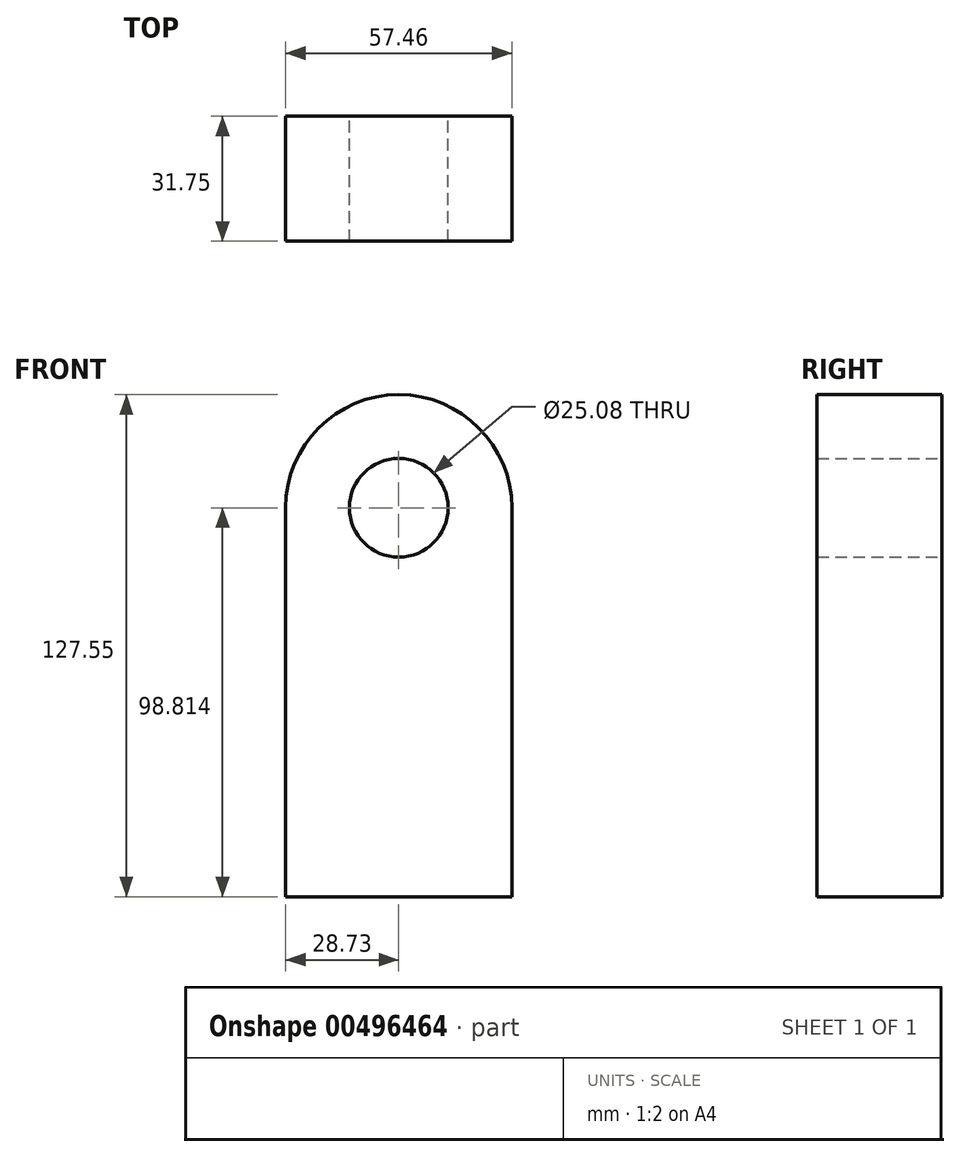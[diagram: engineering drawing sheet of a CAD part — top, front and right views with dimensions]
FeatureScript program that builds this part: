
annotation { "Feature Type Name" : "Feature", "Feature Type Description" : "" }
export const myFeature = defineFeature(function(context is Context, id is Id, definition is map)
    precondition{}
    {
        {
            var Q0;
            Q0=qCreatedBy(makeId("Front.planeOp"),FACE);
            var sketch = newSketch(context, id + "F0", { "sketchPlane" : qUnion([Q0])});
            skLineSegment(sketch, "E0.top", {"start": v(-28.73, -44.67) * mm, "end": v(28.73, -44.67) * mm});
            skLineSegment(sketch, "E0.left", {"start": v(-28.73, 54.14) * mm, "end": v(-28.73, -44.67) * mm});
            skLineSegment(sketch, "E0.right", {"start": v(28.73, 54.14) * mm, "end": v(28.73, -44.67) * mm});
            skPoint(sketch, "E0.middle", {"position": v(0, 4.74) * mm});
            skArc(sketch, "E1", {"start": v(28.73, 54.14) * mm, "mid": v(0, 82.88) * mm, "end": v(-28.73, 54.14) * mm});
            skCircle(sketch, "E2", {"center": v(0, 54.14) * mm, "radius": 12.54 * mm});
            skSolve(sketch);
        }
        {
            var Q0;
            Q0=makeQuery(id+"F0.imprint","IMPRINT",FACE,{"disambiguationData":[TD([[makeQuery(id+"F0.imprint","IMPRINT",EDGE,{"derivedFrom":sQuery(id+"F0.wireOp",EDGE,"E0.top")}),1.0]])]});
            extrude(context, id + "F1", {"entities" : qUnion([Q0]), "depth" : 31.75 * mm});
        }
    });
